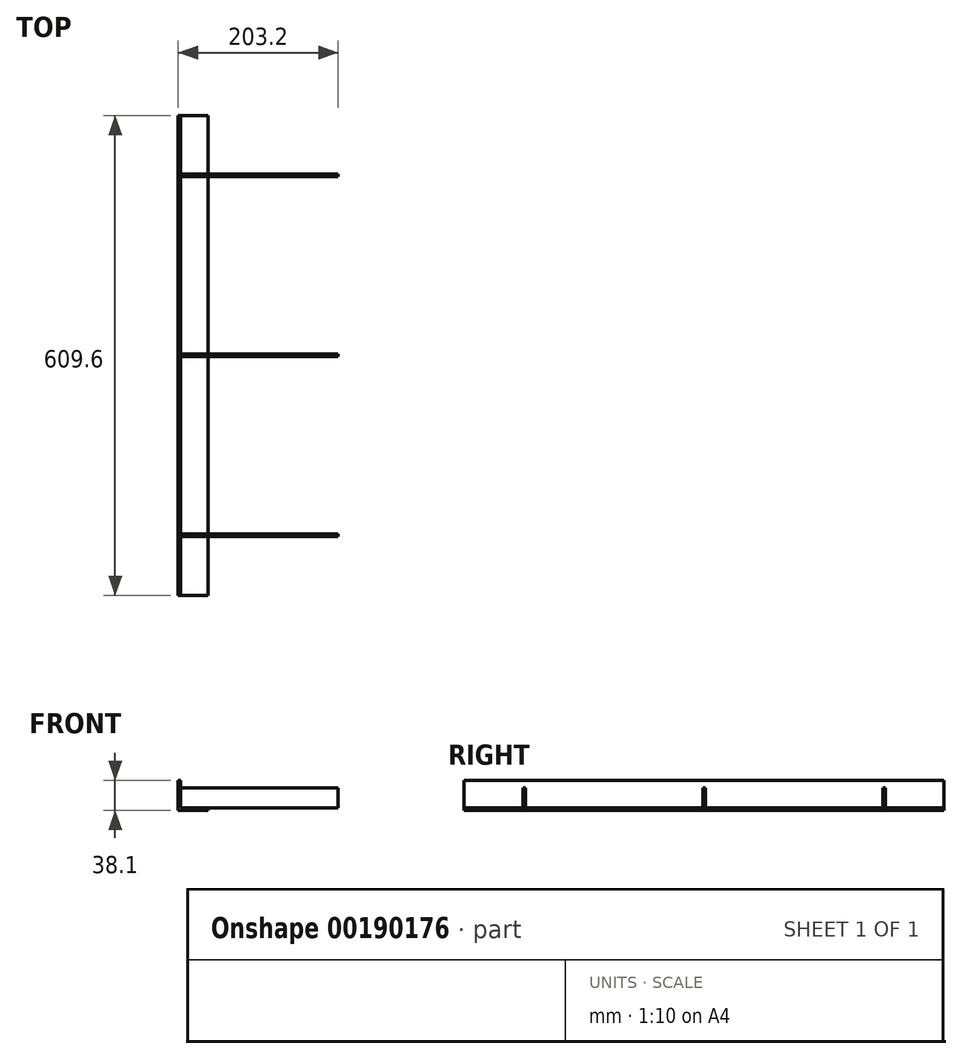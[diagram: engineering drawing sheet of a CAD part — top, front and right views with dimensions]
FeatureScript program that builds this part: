
annotation { "Feature Type Name" : "Feature", "Feature Type Description" : "" }
export const myFeature = defineFeature(function(context is Context, id is Id, definition is map)
    precondition{}
    {
        {
            var Q0;
            Q0=qCreatedBy(makeId("Front.planeOp"),FACE);
            var sketch = newSketch(context, id + "F0", { "sketchPlane" : qUnion([Q0])});
            skLineSegment(sketch, "E0.bottom", {"start": v(0, 38.1) * mm, "end": v(3.18, 38.1) * mm});
            skLineSegment(sketch, "E0.left", {"start": v(0, 38.1) * mm, "end": v(0, 0) * mm});
            skLineSegment(sketch, "E0.right", {"start": v(3.17, 38.1) * mm, "end": v(3.18, 3.18) * mm});
            skLineSegment(sketch, "E1.bottom", {"start": v(3.17, 3.18) * mm, "end": v(38.1, 3.18) * mm});
            skLineSegment(sketch, "E1.right", {"start": v(38.1, 3.18) * mm, "end": v(38.1, 0) * mm});
            skLineSegment(sketch, "E2", {"start": v(0, 0) * mm, "end": v(38.1, 0) * mm});
            skSolve(sketch);
        }
        {
            var Q0;
            Q0 = qSketchRegion(id + "F0", true);
            extrude(context, id + "F1", {"entities" : qUnion([Q0]), "depth" : 609.6 * mm});
        }
        {
            var Q0;
            Q0=qCreatedBy(makeId("Right.planeOp"),FACE);
            var sketch = newSketch(context, id + "F2", { "sketchPlane" : qUnion([Q0])});
            skLineSegment(sketch, "E3.bottom", {"start": v(-77.79, 3.18) * mm, "end": v(-74.61, 3.18) * mm});
            skLineSegment(sketch, "E3.top", {"start": v(-77.79, 28.58) * mm, "end": v(-74.61, 28.58) * mm});
            skLineSegment(sketch, "E3.left", {"start": v(-77.79, 3.18) * mm, "end": v(-77.79, 28.58) * mm});
            skLineSegment(sketch, "E3.right", {"start": v(-74.61, 3.18) * mm, "end": v(-74.61, 28.58) * mm});
            skPoint(sketch, "E4", {"position": v(-533.4, 28.58) * mm});
            skPoint(sketch, "E5.1.0.0", {"position": v(-304.8, 28.58) * mm});
            skPoint(sketch, "E5.2.0.0", {"position": v(-76.2, 28.58) * mm});
            skLineSegment(sketch, "E5.direction1", {"start": v(-533.4, 28.58) * mm, "end": v(-304.8, 28.58) * mm, "construction": true});
            skLineSegment(sketch, "E6.bottom", {"start": v(-306.39, 3.18) * mm, "end": v(-303.21, 3.18) * mm});
            skLineSegment(sketch, "E6.top", {"start": v(-306.39, 28.58) * mm, "end": v(-303.21, 28.58) * mm});
            skLineSegment(sketch, "E6.left", {"start": v(-306.39, 3.18) * mm, "end": v(-306.39, 28.58) * mm});
            skLineSegment(sketch, "E6.right", {"start": v(-303.21, 3.18) * mm, "end": v(-303.21, 28.58) * mm});
            skLineSegment(sketch, "E7.bottom", {"start": v(-534.99, 3.18) * mm, "end": v(-531.81, 3.18) * mm});
            skLineSegment(sketch, "E7.top", {"start": v(-534.99, 28.58) * mm, "end": v(-531.81, 28.58) * mm});
            skLineSegment(sketch, "E7.left", {"start": v(-534.99, 3.18) * mm, "end": v(-534.99, 28.58) * mm});
            skLineSegment(sketch, "E7.right", {"start": v(-531.81, 3.18) * mm, "end": v(-531.81, 28.58) * mm});
            skSolve(sketch);
        }
        {
            var Q0;
            Q0 = qSketchRegion(id + "F2", true);
            extrude(context, id + "F3", {"entities" : qUnion([Q0]), "operationType" : NewBodyOperationType.ADD, "depth" : 203.2 * mm});
        }
    });
